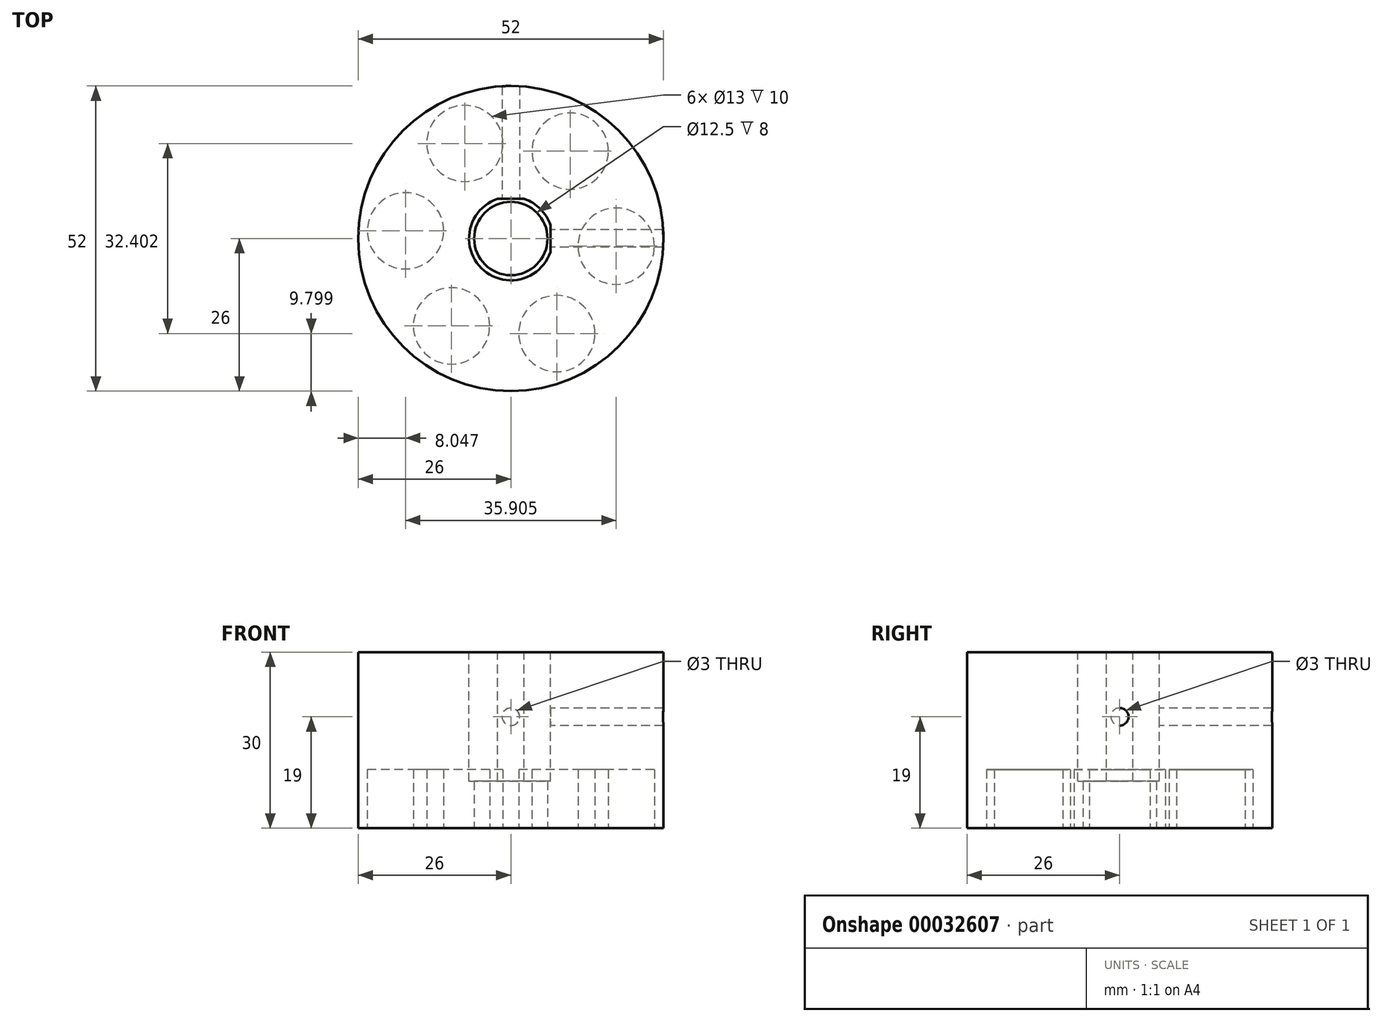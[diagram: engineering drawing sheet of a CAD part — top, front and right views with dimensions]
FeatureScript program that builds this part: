
annotation { "Feature Type Name" : "Feature", "Feature Type Description" : "" }
export const myFeature = defineFeature(function(context is Context, id is Id, definition is map)
    precondition{}
    {
        {
            var Q0;
            Q0=qCreatedBy(makeId("Top.planeOp"),FACE);
            var sketch = newSketch(context, id + "F0", { "sketchPlane" : qUnion([Q0])});
            skCircle(sketch, "E0", {"center": v(0, 0) * mm, "radius": 26 * mm});
            skCircle(sketch, "E1", {"center": v(0, 0) * mm, "radius": 6.25 * mm});
            skSolve(sketch);
        }
        {
            var Q0;
            Q0=makeQuery(id+"F0.imprint","IMPRINT",FACE,{"disambiguationData":[TD([[makeQuery(id+"F0.imprint","IMPRINT",EDGE,{"derivedFrom":sQuery(id+"F0.wireOp",EDGE,"E0")}),1.0]])]});
            var Q1;
            Q1=makeQuery(id+"F0.imprint","IMPRINT",FACE,{"disambiguationData":[TD([[makeQuery(id+"F0.imprint","IMPRINT",EDGE,{"derivedFrom":sQuery(id+"F0.wireOp",EDGE,"E1")}),1.0]])]});
            extrude(context, id + "F1", {"entities" : qUnion([Q0, Q1]), "depth" : 30 * mm});
        }
        {
            var Q0;
            Q0=makeQuery(id+"F1.opExtrude","CAP_FACE",FACE,{"disambiguationData":[OSD([sQuery(id+"F0.wireOp",EDGE,"E0"),sQuery(id+"F0.wireOp",EDGE,"E1")])],"isStart":false});
            var sketch = newSketch(context, id + "F2", { "sketchPlane" : qUnion([Q0])});
            skCircle(sketch, "E2", {"center": v(0, 0) * mm, "radius": 7.12 * mm});
            skLineSegment(sketch, "E3", {"start": v(0, 0) * mm, "end": v(0, 6.75) * mm, "construction": true});
            skLineSegment(sketch, "E4", {"start": v(0, 0) * mm, "end": v(6.75, 0) * mm, "construction": true});
            skLineSegment(sketch, "E5.bottom", {"start": v(6.75, 6.75) * mm, "end": v(-6.75, 6.75) * mm});
            skLineSegment(sketch, "E5.top", {"start": v(6.75, -6.75) * mm, "end": v(-6.75, -6.75) * mm});
            skLineSegment(sketch, "E5.left", {"start": v(6.75, 6.75) * mm, "end": v(6.75, -6.75) * mm});
            skLineSegment(sketch, "E5.right", {"start": v(-6.75, 6.75) * mm, "end": v(-6.75, -6.75) * mm});
            skSolve(sketch);
        }
        {
            var Q0;
            Q0=makeQuery(id+"F0.imprint","IMPRINT",FACE,{"disambiguationData":[TD([[makeQuery(id+"F0.imprint","IMPRINT",EDGE,{"derivedFrom":sQuery(id+"F0.wireOp",EDGE,"E1")}),1.0]])]});
            extrude(context, id + "F3", {"entities" : qUnion([Q0]), "operationType" : NewBodyOperationType.REMOVE, "depth" : 25 * mm});
        }
        {
            var Q0;
            {var subQ1=sQuery(id+"F2.wireOp",EDGE,"E2");var subQ9=sQuery(id+"F2.wireOp",EDGE,"E5.bottom");var subQ11=makeQuery(id+"F2.imprint","INTERSECT",VERTEX,{"disambiguationData":[OD(0.0)],"derivedFrom":[subQ1,subQ9]});Q0=makeQuery(id+"F2.imprint","IMPRINT",FACE,{"disambiguationData":[TD([[makeQuery(id+"F2.imprint","IMPRINT",EDGE,{"disambiguationData":[TD([[subQ11,1.0]])],"derivedFrom":subQ1}),1.0]])]});}
            var Q1;
            {var subQ0=sQuery(id+"F2.wireOp",EDGE,"E5.right");var subQ1=sQuery(id+"F2.wireOp",EDGE,"E2");var subQ2=makeQuery(id+"F2.imprint","INTERSECT",VERTEX,{"disambiguationData":[OD(0.0)],"derivedFrom":[subQ1,subQ0]});Q1=makeQuery(id+"F2.imprint","IMPRINT",FACE,{"disambiguationData":[TD([[makeQuery(id+"F2.imprint","IMPRINT",EDGE,{"disambiguationData":[TD([[subQ2,-1.0]])],"derivedFrom":subQ1}),1.0]])]});}
            var Q2;
            {var subQ0=sQuery(id+"F2.wireOp",EDGE,"E5.top");var subQ1=sQuery(id+"F2.wireOp",EDGE,"E2");var subQ2=makeQuery(id+"F2.imprint","INTERSECT",VERTEX,{"disambiguationData":[OD(0.0)],"derivedFrom":[subQ1,subQ0]});Q2=makeQuery(id+"F2.imprint","IMPRINT",FACE,{"disambiguationData":[TD([[makeQuery(id+"F2.imprint","IMPRINT",EDGE,{"disambiguationData":[TD([[subQ2,-1.0]])],"derivedFrom":subQ1}),1.0]])]});}
            extrude(context, id + "F4", {"entities" : qUnion([Q0, Q1, Q2]), "operationType" : NewBodyOperationType.REMOVE, "oppositeDirection" : true, "depth" : 22 * mm});
        }
        {
            var Q0;
            Q0=makeQuery(id+"F4.boolean.opBoolean","COPY",FACE,{"derivedFrom":makeQuery(id+"F4.opExtrude","SWEPT_FACE",FACE,{"disambiguationData":[OSD([sQuery(id+"F2.wireOp",EDGE,"E5.left")])]})});
            var sketch = newSketch(context, id + "F5", { "sketchPlane" : qUnion([Q0])});
            skCircle(sketch, "E6", {"center": v(0, 19) * mm, "radius": 1.5 * mm});
            skPoint(sketch, "E6.centerSnap0", {"position": v(0, 30) * mm});
            skPoint(sketch, "E6.centerSnap1", {"position": v(-2.28, 19) * mm});
            skSolve(sketch);
        }
        {
            var Q0;
            Q0=makeQuery(id+"F5.imprint","IMPRINT",FACE,{"disambiguationData":[TD([[makeQuery(id+"F5.imprint","IMPRINT",EDGE,{"derivedFrom":sQuery(id+"F5.wireOp",EDGE,"E6")}),1.0]])]});
            extrude(context, id + "F6", {"entities" : qUnion([Q0]), "operationType" : NewBodyOperationType.REMOVE, "oppositeDirection" : true, "depth" : 25 * mm});
        }
        {
            var Q0;
            Q0=makeQuery(id+"F4.boolean.opBoolean","COPY",FACE,{"derivedFrom":makeQuery(id+"F4.opExtrude","SWEPT_FACE",FACE,{"disambiguationData":[OSD([sQuery(id+"F2.wireOp",EDGE,"E5.bottom")])]})});
            var sketch = newSketch(context, id + "F7", { "sketchPlane" : qUnion([Q0])});
            skCircle(sketch, "E7", {"center": v(0, 19) * mm, "radius": 1.5 * mm});
            skPoint(sketch, "E7.centerSnap0", {"position": v(0, 8) * mm});
            skPoint(sketch, "E7.centerSnap1", {"position": v(2.28, 19) * mm});
            skSolve(sketch);
        }
        {
            var Q0;
            Q0=makeQuery(id+"F7.imprint","IMPRINT",FACE,{"disambiguationData":[TD([[makeQuery(id+"F7.imprint","IMPRINT",EDGE,{"derivedFrom":sQuery(id+"F7.wireOp",EDGE,"E7")}),1.0]])]});
            extrude(context, id + "F8", {"entities" : qUnion([Q0]), "operationType" : NewBodyOperationType.REMOVE, "oppositeDirection" : true, "depth" : 25 * mm});
        }
        {
            var Q0;
            Q0=makeQuery(id+"F0.imprint","IMPRINT",FACE,{"disambiguationData":[TD([[makeQuery(id+"F0.imprint","IMPRINT",EDGE,{"derivedFrom":sQuery(id+"F0.wireOp",EDGE,"E0")}),1.0]])]});
            var sketch = newSketch(context, id + "F9", { "sketchPlane" : qUnion([Q0])});
            skCircle(sketch, "E8.cCircle", {"center": v(0, 0) * mm, "radius": 18 * mm, "construction": true});
            skLineSegment(sketch, "E8.0", {"start": v(10.1, 14.9) * mm, "end": v(17.95, -1.3) * mm, "construction": true});
            skLineSegment(sketch, "E8.1", {"start": v(17.95, -1.3) * mm, "end": v(7.84, -16.2) * mm, "construction": true});
            skLineSegment(sketch, "E8.2", {"start": v(7.84, -16.2) * mm, "end": v(-10.1, -14.9) * mm, "construction": true});
            skLineSegment(sketch, "E8.3", {"start": v(-10.1, -14.9) * mm, "end": v(-17.95, 1.3) * mm, "construction": true});
            skLineSegment(sketch, "E8.4", {"start": v(-17.95, 1.3) * mm, "end": v(-7.84, 16.2) * mm, "construction": true});
            skLineSegment(sketch, "E8.5", {"start": v(-7.84, 16.2) * mm, "end": v(10.1, 14.9) * mm, "construction": true});
            skCircle(sketch, "E9", {"center": v(-17.95, 1.3) * mm, "radius": 6.5 * mm});
            skCircle(sketch, "E10", {"center": v(-10.1, -14.9) * mm, "radius": 6.5 * mm});
            skCircle(sketch, "E11", {"center": v(7.84, -16.2) * mm, "radius": 6.5 * mm});
            skCircle(sketch, "E12", {"center": v(17.95, -1.3) * mm, "radius": 6.5 * mm});
            skCircle(sketch, "E13", {"center": v(10.1, 14.9) * mm, "radius": 6.5 * mm});
            skCircle(sketch, "E14", {"center": v(-7.84, 16.2) * mm, "radius": 6.5 * mm});
            skSolve(sketch);
        }
        {
            var Q0;
            Q0=makeQuery(id+"F9.imprint","IMPRINT",FACE,{"disambiguationData":[TD([[makeQuery(id+"F9.imprint","IMPRINT",EDGE,{"derivedFrom":sQuery(id+"F9.wireOp",EDGE,"E14")}),1.0]])]});
            var Q1;
            Q1=makeQuery(id+"F9.imprint","IMPRINT",FACE,{"disambiguationData":[TD([[makeQuery(id+"F9.imprint","IMPRINT",EDGE,{"derivedFrom":sQuery(id+"F9.wireOp",EDGE,"E13")}),1.0]])]});
            var Q2;
            Q2=makeQuery(id+"F9.imprint","IMPRINT",FACE,{"disambiguationData":[TD([[makeQuery(id+"F9.imprint","IMPRINT",EDGE,{"derivedFrom":sQuery(id+"F9.wireOp",EDGE,"E12")}),1.0]])]});
            var Q3;
            Q3=makeQuery(id+"F9.imprint","IMPRINT",FACE,{"disambiguationData":[TD([[makeQuery(id+"F9.imprint","IMPRINT",EDGE,{"derivedFrom":sQuery(id+"F9.wireOp",EDGE,"E11")}),1.0]])]});
            var Q4;
            Q4=makeQuery(id+"F9.imprint","IMPRINT",FACE,{"disambiguationData":[TD([[makeQuery(id+"F9.imprint","IMPRINT",EDGE,{"derivedFrom":sQuery(id+"F9.wireOp",EDGE,"E10")}),1.0]])]});
            var Q5;
            Q5=makeQuery(id+"F9.imprint","IMPRINT",FACE,{"disambiguationData":[TD([[makeQuery(id+"F9.imprint","IMPRINT",EDGE,{"derivedFrom":sQuery(id+"F9.wireOp",EDGE,"E9")}),1.0]])]});
            extrude(context, id + "F10", {"entities" : qUnion([Q0, Q1, Q2, Q3, Q4, Q5]), "operationType" : NewBodyOperationType.REMOVE, "depth" : 10 * mm});
        }
    });
